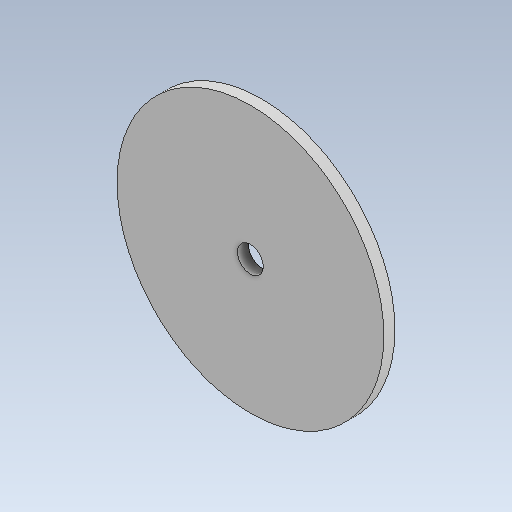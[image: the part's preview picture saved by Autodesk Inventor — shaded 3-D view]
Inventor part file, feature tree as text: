
AUTODESK INVENTOR PART (.ipt)
format: ipt  version: 2020 (Build 240168000, 168)  size: 92,160 bytes
history: native  units: mm
features: extrude x1, sketch x1
ambient origin geometry x8: Origin, YZ Plane, XZ Plane, XY Plane, X Axis, Y Axis, Z Axis, Center Point
bodies: Solid1 (feature_tree)
feature tree (2):
  extrude  "Extrusion1"  Depth=1.5mm
  sketch  "Sketch1"  dims[d0=36.0mm d1=3.5mm d2=1.5mm d3=0.0mm]
